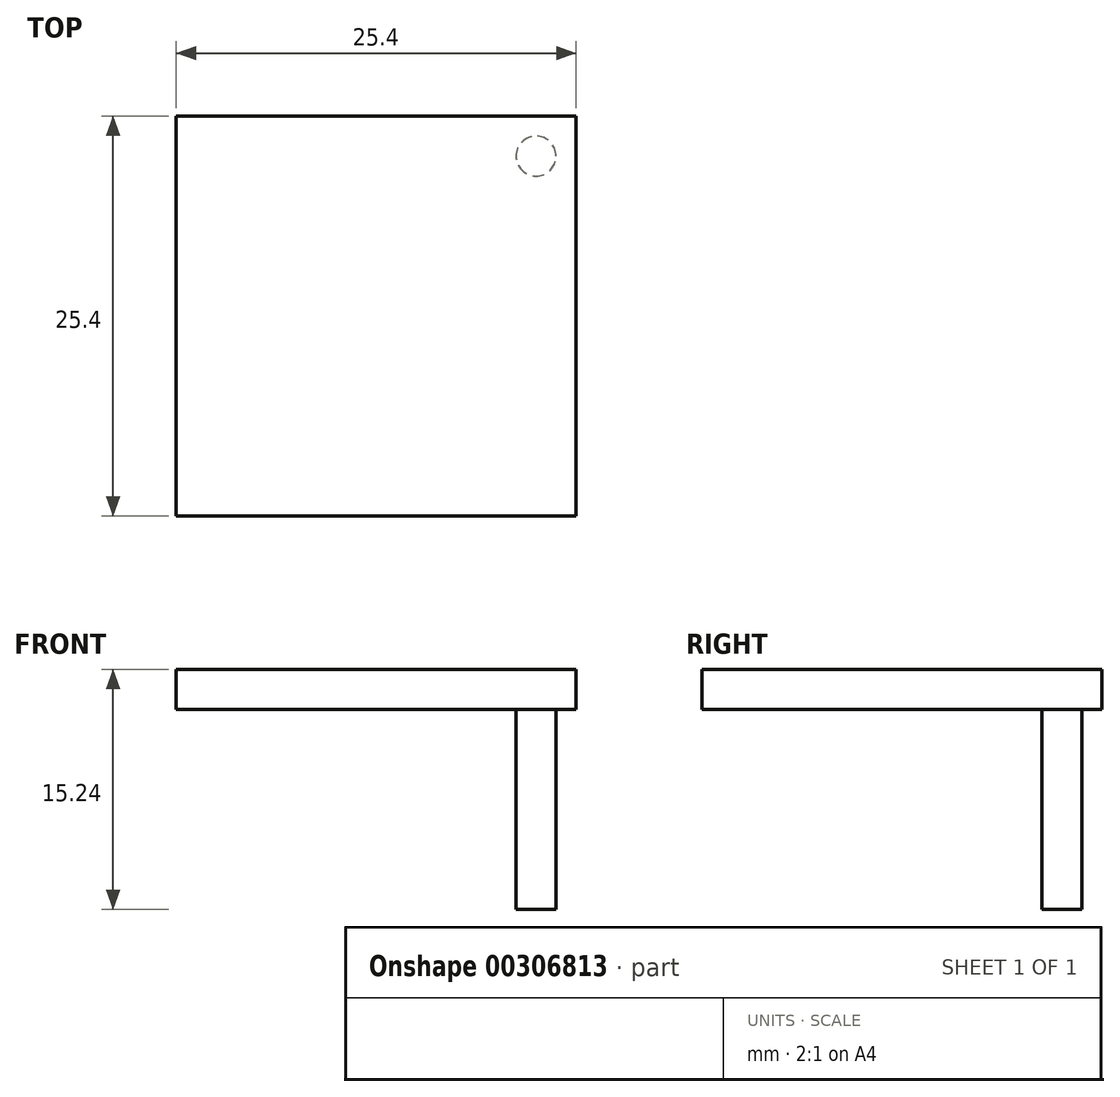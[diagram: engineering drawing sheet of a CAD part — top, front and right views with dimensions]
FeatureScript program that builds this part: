
annotation { "Feature Type Name" : "Feature", "Feature Type Description" : "" }
export const myFeature = defineFeature(function(context is Context, id is Id, definition is map)
    precondition{}
    {
        {
            var Q0;
            Q0=qCreatedBy(makeId("Top.planeOp"),FACE);
            var sketch = newSketch(context, id + "F0", { "sketchPlane" : qUnion([Q0])});
            skLineSegment(sketch, "E0", {"start": v(0, 0) * mm, "end": v(0, 25.4) * mm});
            skLineSegment(sketch, "E1", {"start": v(0, 25.4) * mm, "end": v(25.4, 25.4) * mm});
            skLineSegment(sketch, "E2", {"start": v(25.4, 25.4) * mm, "end": v(25.4, 0) * mm});
            skLineSegment(sketch, "E3", {"start": v(25.4, 0) * mm, "end": v(0, 0) * mm});
            skSolve(sketch);
        }
        {
            var Q0;
            Q0=makeQuery(id+"F0.imprint","IMPRINT",FACE,{"disambiguationData":[TD([[makeQuery(id+"F0.imprint","IMPRINT",EDGE,{"derivedFrom":sQuery(id+"F0.wireOp",EDGE,"E0")}),-1.0]])]});
            extrude(context, id + "F1", {"entities" : qUnion([Q0]), "depth" : 2.54 * mm});
        }
        {
            var Q0;
            Q0=makeQuery(id+"F1.opExtrude","CAP_FACE",FACE,{"disambiguationData":[OSD([sQuery(id+"F0.wireOp",EDGE,"E0"),sQuery(id+"F0.wireOp",EDGE,"E1"),sQuery(id+"F0.wireOp",EDGE,"E2"),sQuery(id+"F0.wireOp",EDGE,"E3")])],"isStart":true});
            var sketch = newSketch(context, id + "F2", { "sketchPlane" : qUnion([Q0])});
            skCircle(sketch, "E4", {"center": v(22.86, -22.86) * mm, "radius": 1.27 * mm});
            skSolve(sketch);
        }
        {
            var Q0;
            Q0=makeQuery(id+"F2.imprint","IMPRINT",FACE,{"disambiguationData":[TD([[makeQuery(id+"F2.imprint","IMPRINT",EDGE,{"derivedFrom":sQuery(id+"F2.wireOp",EDGE,"E4")}),1.0]])]});
            extrude(context, id + "F3", {"entities" : qUnion([Q0]), "operationType" : NewBodyOperationType.ADD, "depth" : 12.7 * mm});
        }
    });
